# Revit family: Lighting-UrbanLighting-GEWISS-POINT-LED_GARDEN_LIGHTING
name_source: partatom
category: Apparecchi per illuminazione
units: mm (PartAtom-declared; Revit-internal decimal feet)

## family parameters
Condiviso = No
Host = Superficie
Numero OmniClass = 23.80.70.00
Punto di calcolo locali = Sì
Quota connettore circolare = Usa diametro
Sorgente d'illuminazione = No
Taglio con vuoti quando caricato = No
Tipo di parte = Normale
Titolo OmniClass = Lighting

## types (6) — shared parameters
2D LAT = 2D - POINT : 006
Altezza = 473 mm
Carico apparente = 4 VA
Catalogue = LIGHTING
Colour temperature = 3000K
Commenti sul wattaggio = 4W
Glow Wire Test = 650°C
IDF = cf99eae4-1613-4a01-afce-b88c81c82e99
IDT = f2a9305b-c3d1-4dd3-b135-09b9879f617e
Immagine tipo = GW82006.jpg
Lamp = DR
Lampada = DR
No. of lamps: = 1
Numero di poli = 2
Produttore = GEWISS S.p.A.
Prospetto di default = 1219 mm
Raggio = 69 mm
Raggio int = 45 mm  [stored 0.147638 ft]
SEO = Pole
Struttura = GEWISS - Grigio Grafite
Technical sheet = https://www.gewiss.com
URL = https://www.gewiss.com
Version file RFA = 20.11
Vetro = GEWISS - vetro acceso
Voltage = 230 V - 50 Hz
Voltaggio = 230 V

## per-type parameters (varying)
| type | Application | Catalogue Range | Colour | Colour temperature: | Descrizione | EAN code | Efficiency class of integrated LEDs | Electrocod | Height (mm) | IP degree | Insulation class | Lamp holder | Lamp power | Light pollution | Light pollution: | Modello | No. of lamps | Shock resistance | Type of light source | Warranty |
| GW82016B - POINT GR.6W E27 DR 3000K BLUE | External | POINT | Midnight blue |  | POINT GR.6W E27 DR 3000K BLUE | 8011564869035 | D ÷ A+ | 2442 | 550 | IP55 | II | E27 | 6W | 25% | 25% | GW82016B | 1 | IK10 | A+ | Can be extended |
| GW82011B - POINT PI.4W E14 DR 3000K BLUE | External | POINT | Midnight blue |  | POINT PI.4W E14 DR 3000K BLUE | 8011564869028 | D ÷ A+ | 2442 | 473 | IP55 | II | E14 | 4W | 25% | 25% | GW82011B | 1 | IK10 | A+ | Can be extended |
| GW82011G - POINT PI.4W E14 DR 3000K GRAP. GREY | External | POINT | Graphite grey |  | POINT PI.4W E14 DR 3000K GRAP. GREY | 8011564869004 | D ÷ A+ | 2442 | 473 | IP55 | II | E14 | 4W | 25% | 25% | GW82011G | 1 | IK10 | A+ | Can be extended |
| GW82018B - POINT 780MM 6W E27 DR 3000K BLU |  |  | BlueGreen | 3000 K | POINT 780MM 6W E27 DR 3000K BLU |  |  | 2424 | 780 |  |  | E27 | 11W |  |  | GW82018B |  |  |  |  |
| GW82016G - POINT GR.6W E27 DR 3000K GRAP. GREY | External | POINT | Graphite grey |  | POINT GR.6W E27 DR 3000K GRAP. GREY | 8011564869011 | D ÷ A+ | 2442 | 550 | IP55 | II | E27 | 6W | 25% | 25% | GW82016G | 1 | IK10 | A+ | Can be extended |
| GW82018G - POINT 780MM 6W E27 DR 3000K GRIGIO |  |  | Graphite grey | 3000 K | POINT 780MM 6W E27 DR 3000K GRIGIO |  |  | 2424 | 780 |  |  | E27 | 11W |  |  | GW82018G |  |  |  |  |

note: [stored X ft] marks values corroborated as IEEE doubles in the binary element streams (Revit-internal decimal feet)

## geometry (parser evidence)
native form markers: Blend x409
no freeform markers — native parametric forms only
